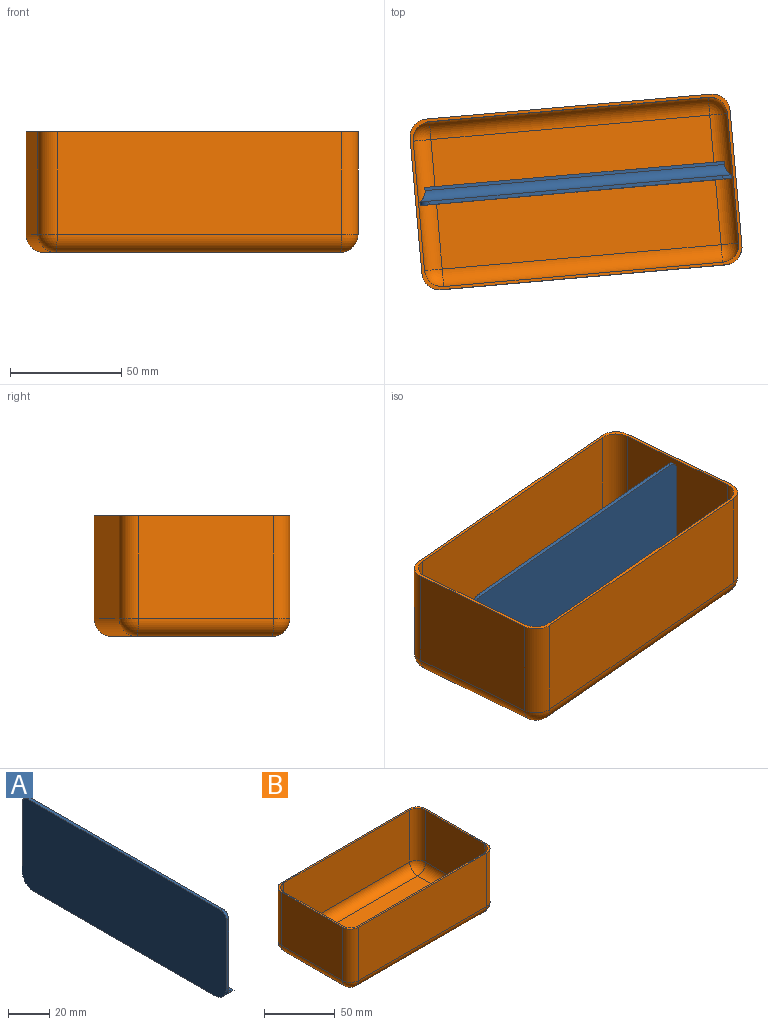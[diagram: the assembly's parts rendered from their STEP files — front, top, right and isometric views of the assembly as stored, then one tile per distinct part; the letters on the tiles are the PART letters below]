
ASSEMBLY  parts=2 mates=1
PART A: 13 faces, bbox 8x140.7x53 mm
  f0: plane 124.7x8mm, normal (0,0,-1), area 997.6mm2, adj f1,f5,f8,f9
  f1: plane 135.28x2mm, normal (1,0,0), area 263.9mm2, adj f0,f2,f8,f9
  f2: plane 135.28x1.4mm, normal (0,0,1), area 189.4mm2, adj f1,f8,f9,f10
  f3: plane 140.7x46mm, normal (1,0,0), area 6465.3mm2, adj f4,f6,f7,f8,f9,f10,f11,f12
  f4: plane 132.7x1.6mm, normal (0,0,1), area 212.3mm2, adj f3,f5,f11,f12
  f5: plane 140.7x53mm, normal (-1,0,0), area 7422.8mm2, adj f0,f4,f6,f7,f8,f9,f11,f12
  f6: plane 41x1.6mm, normal (0,-1,0), area 65.6mm2, adj f3,f5,f9,f12
  f7: plane 41x1.6mm, normal (0,1,0), area 65.6mm2, adj f3,f5,f8,f11
  f8: cylinder r=8mm len=8mm, axis (1,0,0), area 64.1mm2, adj f0,f1,f2,f3,f5,f7,f10
  f9: cylinder r=8mm len=8mm, axis (-1,0,0), area 64.1mm2, adj f0,f1,f2,f3,f5,f6,f10
  f10: cylinder r=5mm len=140.57mm, axis (0,1,0), area 1082.8mm2, adj f2,f3,f8,f9
  f11: cylinder r=4mm len=4mm, axis (-1,0,0), area 10.1mm2, adj f3,f4,f5,f7
  f12: cylinder r=4mm len=4mm, axis (1,0,0), area 10.1mm2, adj f3,f4,f5,f6
PART B: 35 faces, bbox 144.6x77.1x54.3 mm
  f0: plane 61.1x46.3mm, normal (1,0,0), area 2828.9mm2, adj f8,f13,f16,f26
  f1: plane 128.6x46.3mm, normal (0,1,0), area 5954.2mm2, adj f8,f13,f14,f22
  f2: plane 61.1x46.3mm, normal (-1,0,0), area 2828.9mm2, adj f8,f14,f15,f19
  f3: plane 58.5x45mm, normal (1,0,0), area 2632.5mm2, adj f8,f9,f12,f32
  f4: plane 126x45mm, normal (0,-1,0), area 5670mm2, adj f8,f9,f10,f28
  f5: plane 58.5x45mm, normal (-1,0,0), area 2632.5mm2, adj f8,f10,f11,f29
  f6: plane 126x45mm, normal (0,1,0), area 5670mm2, adj f8,f11,f12,f33
  f7: plane 128.6x46.3mm, normal (0,-1,0), area 5954.2mm2, adj f8,f15,f16,f23
  f8: plane 144.6x77.1mm, normal (0,0,1), area 569.7mm2, adj f0,f1,f2,f3,f4,f5,f6,f7
  f9: cylinder r=8mm len=45mm, axis (0,0,-1), area 565.5mm2, adj f3,f4,f8,f30
  f10: cylinder r=8mm len=45mm, axis (0,0,1), area 565.5mm2, adj f4,f5,f8,f27
  f11: cylinder r=8mm len=45mm, axis (0,0,-1), area 565.5mm2, adj f5,f6,f8,f31
  f12: cylinder r=8mm len=45mm, axis (0,0,1), area 565.5mm2, adj f3,f6,f8,f34
  f13: cylinder r=8mm len=46.3mm, axis (0,0,-1), area 581.8mm2, adj f0,f1,f8,f24
  f14: cylinder r=8mm len=46.3mm, axis (0,0,1), area 581.8mm2, adj f1,f2,f8,f20
  f15: cylinder r=8mm len=46.3mm, axis (0,0,-1), area 581.8mm2, adj f2,f7,f8,f21
  f16: cylinder r=8mm len=46.3mm, axis (0,0,1), area 581.8mm2, adj f0,f7,f8,f25
  f17: plane 126x58.5mm, normal (0,0,1), area 7371mm2, adj f28,f29,f32,f33
  f18: plane 128.6x61.1mm, normal (0,0,-1), area 7857.5mm2, adj f19,f22,f23,f26
  f19: cylinder r=8mm len=61.1mm, axis (0,-1,0), area 767.8mm2, adj f2,f18,f20,f21
  f20: sphere r=8mm, area 100.5mm2, adj f14,f19,f22
  f21: sphere r=8mm, area 100.5mm2, adj f15,f19,f23
  f22: cylinder r=8mm len=128.6mm, axis (-1,0,0), area 1616mm2, adj f1,f18,f20,f24
  f23: cylinder r=8mm len=128.6mm, axis (1,0,0), area 1616mm2, adj f7,f18,f21,f25
  f24: sphere r=8mm, area 100.5mm2, adj f13,f22,f26
  f25: sphere r=8mm, area 100.5mm2, adj f16,f23,f26
  f26: cylinder r=8mm len=61.1mm, axis (0,1,0), area 767.8mm2, adj f0,f18,f24,f25
  f27: sphere r=8mm, area 100.5mm2, adj f10,f28,f29
  f28: cylinder r=8mm len=126mm, axis (1,0,0), area 1583.4mm2, adj f4,f17,f27,f30
  f29: cylinder r=8mm len=58.5mm, axis (0,-1,0), area 735.1mm2, adj f5,f17,f27,f31
  f30: sphere r=8mm, area 100.5mm2, adj f9,f28,f32
  f31: sphere r=8mm, area 100.5mm2, adj f11,f29,f33
  f32: cylinder r=8mm len=58.5mm, axis (0,1,0), area 735.1mm2, adj f3,f17,f30,f34
  f33: cylinder r=8mm len=126mm, axis (-1,0,0), area 1583.4mm2, adj f6,f17,f31,f34
  f34: sphere r=8mm, area 100.5mm2, adj f12,f32,f33
PLACE A rot(axis=(0,0,1),95deg) t=(-0.85,4.73,-15.91)mm
PLACE B rot(axis=(0,0,1),5deg) t=(-0.85,4.73,-15.91)mm
MATE revolute A.f0 <-> B.f17  axis (0,0,1) through (-0.85,4.73,-15.91)mm
